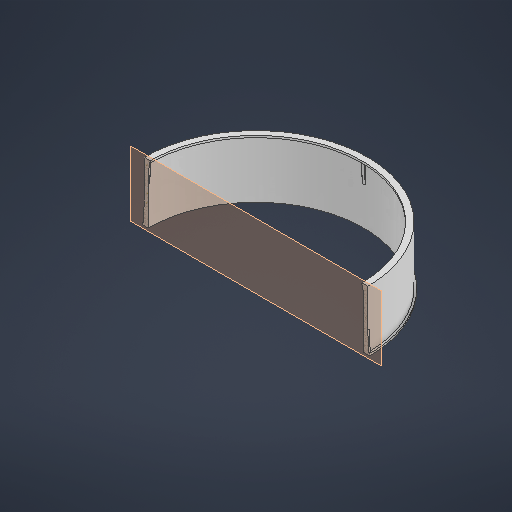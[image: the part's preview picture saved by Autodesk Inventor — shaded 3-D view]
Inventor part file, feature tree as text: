
AUTODESK INVENTOR PART (.ipt)
format: ipt  version: 2025 (Build 290162000, 162)  size: 547,328 bytes
history: native  units: in
note: dims shown in document units (in); Inventor stores cm internally (conversion verified against a paired STEP export)
features: rib x44, sketch x28, other x12, extrude x5, plane x1
ambient origin geometry x8: Origin, YZ Plane, XZ Plane, XY Plane, X Axis, Y Axis, Z Axis, Center Point
bodies: Solid1 (feature_tree)
feature tree (90):
  other  "Table"
  other  "C .Replace - 01"
  other  "C .Replace - 02"
  other  "C .Replace - 03"
  other  "C .Replace - 04"
  other  "C .Replace - 05"
  other  "C .Replace - 06"
  other  "C .Replace - 07"
  other  "C .Replace - 08"
  other  "C .Replace - 09"
  other  "C .Replace - 10"
  other  "C .Replace - Face"
  sketch  "Sketch1"  dims[d5=0.0in d7=0.0in]
  extrude  "Extrusion1"  TaperAngle=0.0deg  [1 undecoded]
  extrude  "Extrusion2"  Depth=10.0394in
  sketch  "Sketch2"  dims[d28=0.1969in d29=3.937in d31=360.0deg]
  extrude  "Extrusion7"  Depth=3.937in TaperAngle=360.0deg
  plane  "Work Plane2"
  extrude  "Extrusion8"  Depth=4.5276in
  extrude  "Extrusion30"  Depth=0.2165in
  sketch  "Sketch26"  dims[d236=0.3937in d237=0.0in]
  sketch  "Sketch27"  dims[d552=0.7874in]
  sketch  "Sketch28"  dims[d553=0.7874in]
  sketch  "Sketch29"  dims[d554=0.0394in d555=0.0394in d556=0.0in d557=0.0in d558=0.0394in d559=0.0394in]
  sketch  "Sketch30"  dims[d560=0.0394in d561=0.0394in d562=0.0in d563=0.0in d564=0.0394in d565=0.0394in]
  sketch  "Sketch32"  dims[d567=0.7874in]
  sketch  "Sketch33"  dims[d568=0.0394in d569=0.0394in d570=0.0in d571=0.0in d572=0.0394in d573=0.0394in]
  sketch  "Sketch34"  dims[d574=0.0394in]
  sketch  "Sketch35"  dims[d575=0.1181in d576=0.0in d577=0.0in d578=0.0394in d579=0.0394in]
  sketch  "Sketch36"  dims[d580=0.7874in]
  sketch  "Sketch37"  dims[d581=0.7874in]
  sketch  "Sketch38"  dims[d582=0.0394in]
  sketch  "Sketch39"  dims[d583=0.1181in d584=0.0in d585=0.0in d586=0.0394in d587=0.0394in]
  sketch  "Sketch40"  dims[d588=0.0394in]
  sketch  "Sketch41"  dims[d589=0.1181in d590=0.0in d591=0.0in d592=0.0394in d593=0.0394in]
  sketch  "Sketch42"  dims[d594=0.7874in]
  sketch  "Sketch43"  dims[d595=0.7874in]
  sketch  "Sketch44"  dims[d596=0.0394in]
  sketch  "Sketch45"  dims[d597=0.1181in d598=0.0in d599=0.0in d600=0.0394in d601=0.0394in]
  sketch  "Sketch46"  dims[d602=0.0394in]
  sketch  "Sketch47"  dims[d603=0.1181in d604=0.0in d605=0.0in d606=0.0394in d607=0.0394in d608=0.7874in d609=0.7874in d610=0.0394in d611=0.1181in d612=0.0in d613=0.0in d614=0.0394in d615=0.0394in d616=0.0394in d617=0.1181in d618=0.0in d619=0.0in d620=0.0394in d621=0.0394in d623=0.7874in d636=0.7874in d637=0.7874in d638=0.0394in d639=0.1181in d640=0.0in d641=0.0in d642=0.0394in d643=0.0394in d644=0.0394in d645=0.1181in d646=0.0in d647=0.0in d648=0.0394in d649=0.0394in d650=0.7874in d651=0.7874in d652=0.0394in d653=0.1181in d654=0.0in d655=0.0in d656=0.0394in d657=0.0394in d658=0.0394in d659=0.1181in d660=0.0in d661=0.0in d662=0.0394in d663=0.0394in d664=0.7874in d665=0.7874in d666=0.0394in d667=0.1181in d668=0.0in d669=0.0in d670=0.0394in d671=0.0394in d672=0.0394in d673=0.1181in d674=0.0in d675=0.0in d676=0.0394in d677=0.0394in d678=0.7874in d679=0.7874in d680=0.0394in d681=0.1181in d682=0.0in d683=0.0in d684=0.0394in d685=0.0394in d686=0.0394in d687=0.1181in d688=0.0in d689=0.0in d690=0.0394in d691=0.0394in d692=0.7874in d693=0.7874in d694=0.0394in d695=0.1181in d696=0.0in d697=0.0in d698=0.0394in d699=0.0394in d700=0.0394in d701=0.1181in d702=0.0in d703=0.0in d704=0.0394in d705=0.0394in d706=0.7874in d720=0.7874in d721=0.7874in d722=0.0394in d723=0.1181in d724=0.0in d725=0.0in d726=0.0394in d727=0.0394in d728=0.0394in d729=0.1181in d730=0.0in d731=0.0in d732=0.0394in d733=0.0394in d734=0.7874in d735=0.7874in d736=0.0394in d737=0.1181in d738=0.0in d739=0.0in d740=0.0394in d741=0.0394in d742=0.0394in d743=0.1181in d744=0.0in d745=0.0in d746=0.0394in d747=0.0394in d748=0.7874in d749=0.7874in d750=0.0394in d751=0.1181in d752=0.0in d753=0.0in d754=0.0394in d755=0.0394in d756=0.0394in d757=0.1181in d758=0.0in d759=0.0in d760=0.0394in d761=0.0394in d762=0.7874in d763=0.7874in d764=0.0394in d765=0.1181in d766=0.0in d767=0.0in d768=0.0394in d769=0.0394in d770=0.0394in d771=0.1181in d772=0.0in d773=0.0in d774=0.0394in d775=0.0394in d776=0.7874in d777=0.7874in d778=0.0394in d779=0.1181in d780=0.0in d781=0.0in d782=0.0394in d783=0.0394in d784=0.0394in d785=0.1181in d786=0.0in d787=0.0in d788=0.0394in d789=0.0394in d790=0.7874in d804=0.7874in d805=0.7874in d806=0.0394in d807=0.1181in d808=0.0in d809=0.0in d810=0.0394in d811=0.0394in d812=0.0394in d813=0.1181in d814=0.0in d815=0.0in d816=0.0394in d817=0.0394in d818=0.7874in d819=0.7874in d820=0.0394in d821=0.1181in d822=0.0in d823=0.0in d824=0.0394in d825=0.0394in d826=0.0394in d827=0.1181in d828=0.0in d829=0.0in d830=0.0394in d831=0.0394in d832=0.7874in d833=0.0394in d834=0.1181in d835=0.0in d836=0.0in d837=0.0394in d838=0.0394in d839=0.0394in d840=0.1181in d841=0.0in d842=0.0in d843=0.0394in d844=0.0394in d845=0.7874in d846=0.0394in d847=0.1181in d848=0.0in d849=0.0in d850=0.0394in d851=0.0394in d852=0.0394in d853=0.1181in d854=0.0in d855=0.0in d856=0.0394in d857=0.0394in d858=0.7874in d859=0.0394in d860=0.0394in d861=0.0in d862=0.0in d863=0.0394in d864=0.0394in d865=0.0394in d866=0.0394in d867=0.0in d868=0.0in d869=0.0394in d870=0.0394in d871=0.7874in d872=0.0394in d873=0.0394in d874=0.0in d875=0.0in d876=0.0394in d877=0.0394in d878=0.0394in d879=0.0394in d880=0.0in d881=0.0in d882=0.0394in d883=0.0394in d884=0.7874in d885=0.0394in d886=0.1181in d887=0.0in d888=0.0in d889=0.0394in d890=0.0394in d891=0.0394in d892=0.1181in d893=0.0in d894=0.0in d895=0.0394in d896=0.0394in d113=0.0197in d114=0.0344in d115=0.0197in d116=0.0344in d167=0.0197in d168=0.0344in d169=0.0197in d170=0.0344in d215=0.0197in d216=0.0344in d217=0.0197in d218=0.0344in d219=0.0in d220=0.0in]
  rib  "Rib46"
  rib  "Rib47"
  sketch  "Sketch31"  dims[d566=0.7874in]
  rib  "Rib48"
  rib  "Rib49"
  rib  "Rib50"
  rib  "Rib51"
  rib  "Rib52"
  rib  "Rib53"
  rib  "Rib92"
  rib  "Rib93"
  rib  "Rib54"
  rib  "Rib55"
  rib  "Rib58"
  rib  "Rib59"
  rib  "Rib60"
  rib  "Rib61"
  rib  "Rib62"
  rib  "Rib63"
  rib  "Rib64"
  rib  "Rib65"
  rib  "Rib66"
  rib  "Rib67"
  rib  "Rib70"
  rib  "Rib71"
  rib  "Rib72"
  rib  "Rib73"
  rib  "Rib74"
  rib  "Rib75"
  rib  "Rib76"
  rib  "Rib77"
  rib  "Rib78"
  rib  "Rib79"
  rib  "Rib82"
  rib  "Rib83"
  rib  "Rib84"
  rib  "Rib85"
  rib  "Rib86"
  rib  "Rib87"
  rib  "Rib88"
  rib  "Rib89"
  rib  "Rib90"
  rib  "Rib91"
  rib  "Rib94"
  rib  "Rib95"
  sketch  "Sketch3"  dims[d33=0.3937in d34=0.0in d52=4.5276in]
  sketch  "Sketch Circular Pattern1"  dims[d18=0.0in d27=10.0394in]
  sketch  "Sketch24"  dims[d232=2.3622in d234=360.0deg]
  sketch  "Sketch Circular Pattern4"  dims[d230=4.0157in d231=0.2165in]
note: 1 required parameter value undecoded (feature->parameter linkage not recoverable at this tier; creation-order binding heuristic only, values carry confidence <= 0.55)
